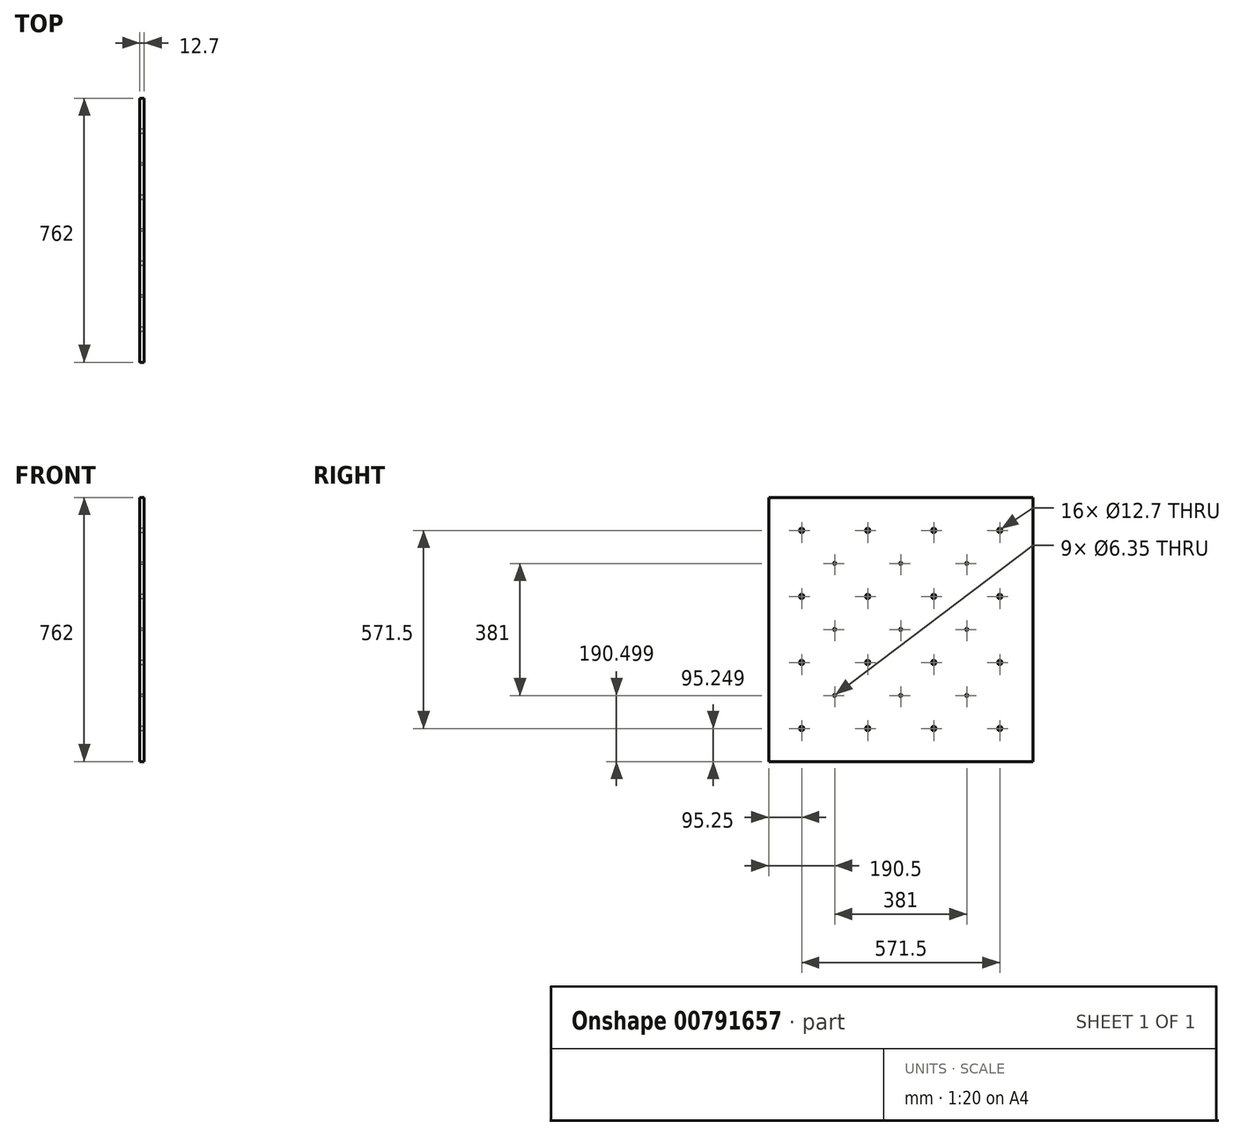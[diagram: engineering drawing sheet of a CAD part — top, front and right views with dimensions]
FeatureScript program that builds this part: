
annotation { "Feature Type Name" : "Feature", "Feature Type Description" : "" }
export const myFeature = defineFeature(function(context is Context, id is Id, definition is map)
    precondition{}
    {
        {
            var Q0;
            Q0=qCreatedBy(makeId("Right.planeOp"),FACE);
            var sketch = newSketch(context, id + "F0", { "sketchPlane" : qUnion([Q0])});
            skLineSegment(sketch, "E0", {"start": v(-381, 347.7) * mm, "end": v(381, 347.7) * mm});
            skLineSegment(sketch, "E1", {"start": v(381, 347.7) * mm, "end": v(381, -414.3) * mm});
            skLineSegment(sketch, "E2", {"start": v(381, -414.3) * mm, "end": v(-381, -414.3) * mm});
            skLineSegment(sketch, "E3", {"start": v(-381, 347.7) * mm, "end": v(-381, -414.3) * mm});
            skPoint(sketch, "E4", {"position": v(-285.75, 252.46) * mm});
            skPoint(sketch, "E5", {"position": v(285.75, 252.46) * mm});
            skPoint(sketch, "E6", {"position": v(-95.25, 252.46) * mm});
            skPoint(sketch, "E7", {"position": v(95.25, 252.46) * mm});
            skPoint(sketch, "E8", {"position": v(-285.75, 61.96) * mm});
            skPoint(sketch, "E9", {"position": v(-285.75, -128.54) * mm});
            skPoint(sketch, "E10", {"position": v(-285.75, -319.04) * mm});
            skPoint(sketch, "E11", {"position": v(-95.25, 61.96) * mm});
            skPoint(sketch, "E12", {"position": v(-95.25, -128.54) * mm});
            skPoint(sketch, "E13", {"position": v(-95.25, -319.04) * mm});
            skPoint(sketch, "E14", {"position": v(95.25, 61.96) * mm});
            skPoint(sketch, "E15", {"position": v(95.25, -128.54) * mm});
            skPoint(sketch, "E16", {"position": v(95.25, -319.04) * mm});
            skPoint(sketch, "E17", {"position": v(285.75, 61.96) * mm});
            skPoint(sketch, "E18", {"position": v(285.75, -128.54) * mm});
            skPoint(sketch, "E19", {"position": v(285.75, -319.04) * mm});
            skCircle(sketch, "E20", {"center": v(-285.75, 252.46) * mm, "radius": 6.35 * mm});
            skCircle(sketch, "E21", {"center": v(-95.25, 252.46) * mm, "radius": 6.35 * mm});
            skCircle(sketch, "E22", {"center": v(95.25, 252.46) * mm, "radius": 6.35 * mm});
            skCircle(sketch, "E23", {"center": v(285.75, 252.46) * mm, "radius": 6.35 * mm});
            skCircle(sketch, "E24", {"center": v(-285.75, 61.96) * mm, "radius": 6.35 * mm});
            skCircle(sketch, "E25", {"center": v(-95.25, 61.96) * mm, "radius": 6.35 * mm});
            skCircle(sketch, "E26", {"center": v(95.25, 61.96) * mm, "radius": 6.35 * mm});
            skCircle(sketch, "E27", {"center": v(285.75, 61.96) * mm, "radius": 6.35 * mm});
            skCircle(sketch, "E28", {"center": v(-285.75, -128.54) * mm, "radius": 6.35 * mm});
            skCircle(sketch, "E29", {"center": v(-95.25, -128.54) * mm, "radius": 6.35 * mm});
            skCircle(sketch, "E30", {"center": v(95.25, -128.54) * mm, "radius": 6.35 * mm});
            skCircle(sketch, "E31", {"center": v(285.75, -128.54) * mm, "radius": 6.35 * mm});
            skCircle(sketch, "E32", {"center": v(285.75, -319.04) * mm, "radius": 6.35 * mm});
            skCircle(sketch, "E33", {"center": v(95.25, -319.04) * mm, "radius": 6.35 * mm});
            skCircle(sketch, "E34", {"center": v(-95.25, -319.04) * mm, "radius": 6.35 * mm});
            skCircle(sketch, "E35", {"center": v(-285.75, -319.04) * mm, "radius": 6.35 * mm});
            skCircle(sketch, "E36", {"center": v(-190.5, 157.2) * mm, "radius": 3.18 * mm});
            skCircle(sketch, "E37", {"center": v(0, 157.2) * mm, "radius": 3.18 * mm});
            skCircle(sketch, "E38", {"center": v(190.5, 157.2) * mm, "radius": 3.18 * mm});
            skCircle(sketch, "E39", {"center": v(190.5, -33.3) * mm, "radius": 3.18 * mm});
            skCircle(sketch, "E40", {"center": v(190.5, -223.8) * mm, "radius": 3.18 * mm});
            skCircle(sketch, "E41", {"center": v(0, -223.8) * mm, "radius": 3.18 * mm});
            skCircle(sketch, "E42", {"center": v(-190.5, -223.8) * mm, "radius": 3.18 * mm});
            skCircle(sketch, "E43", {"center": v(-190.5, -33.3) * mm, "radius": 3.18 * mm});
            skCircle(sketch, "E44", {"center": v(0, -33.3) * mm, "radius": 3.18 * mm});
            skSolve(sketch);
        }
        {
            var Q0;
            Q0=makeQuery(id+"F0.imprint","IMPRINT",FACE,{"disambiguationData":[TD([[makeQuery(id+"F0.imprint","IMPRINT",EDGE,{"derivedFrom":sQuery(id+"F0.wireOp",EDGE,"E0")}),-1.0]])]});
            extrude(context, id + "F1", {"entities" : qUnion([Q0]), "depth" : 12.7 * mm, "offsetDistance" : 25.4 * mm});
        }
        {
            var Q0;
            Q0=sQuery(id+"F0.wireOp",EDGE,"E20");
            extrude(context, id + "F2", {"bodyType" : ToolBodyType.SURFACE, "surfaceEntities" : qUnion([Q0]), "depth" : 368.3 * mm, "offsetDistance" : 25.4 * mm});
        }
        {
            var Q0;
            Q0=sQuery(id+"F0.wireOp",EDGE,"E21");
            extrude(context, id + "F3", {"bodyType" : ToolBodyType.SURFACE, "surfaceEntities" : qUnion([Q0]), "depth" : 368.3 * mm, "offsetDistance" : 25.4 * mm});
        }
        {
            var Q0;
            Q0=sQuery(id+"F0.wireOp",EDGE,"E22");
            var Q1;
            Q1=sQuery(id+"F0.wireOp",EDGE,"E23");
            var Q2;
            Q2=sQuery(id+"F0.wireOp",EDGE,"E24");
            var Q3;
            Q3=sQuery(id+"F0.wireOp",EDGE,"E25");
            var Q4;
            Q4=sQuery(id+"F0.wireOp",EDGE,"E26");
            var Q5;
            Q5=sQuery(id+"F0.wireOp",EDGE,"E27");
            var Q6;
            Q6=sQuery(id+"F0.wireOp",EDGE,"E28");
            var Q7;
            Q7=sQuery(id+"F0.wireOp",EDGE,"E29");
            var Q8;
            Q8=sQuery(id+"F0.wireOp",EDGE,"E30");
            var Q9;
            Q9=sQuery(id+"F0.wireOp",EDGE,"E31");
            var Q10;
            Q10=sQuery(id+"F0.wireOp",EDGE,"E32");
            var Q11;
            Q11=sQuery(id+"F0.wireOp",EDGE,"E33");
            var Q12;
            Q12=sQuery(id+"F0.wireOp",EDGE,"E34");
            var Q13;
            Q13=sQuery(id+"F0.wireOp",EDGE,"E35");
            extrude(context, id + "F4", {"bodyType" : ToolBodyType.SURFACE, "surfaceEntities" : qUnion([Q0, Q1, Q2, Q3, Q4, Q5, Q6, Q7, Q8, Q9, Q10, Q11, Q12, Q13]), "depth" : 368.3 * mm, "offsetDistance" : 25.4 * mm});
        }
        {
            var Q0;
            Q0=sQuery(id+"F0.wireOp",EDGE,"E36");
            var Q1;
            Q1=sQuery(id+"F0.wireOp",EDGE,"E37");
            var Q2;
            Q2=sQuery(id+"F0.wireOp",EDGE,"E38");
            var Q3;
            Q3=sQuery(id+"F0.wireOp",EDGE,"E43");
            var Q4;
            Q4=sQuery(id+"F0.wireOp",EDGE,"E44");
            var Q5;
            Q5=sQuery(id+"F0.wireOp",EDGE,"E39");
            var Q6;
            Q6=sQuery(id+"F0.wireOp",EDGE,"E40");
            var Q7;
            Q7=sQuery(id+"F0.wireOp",EDGE,"E41");
            var Q8;
            Q8=sQuery(id+"F0.wireOp",EDGE,"E42");
            extrude(context, id + "F5", {"bodyType" : ToolBodyType.SURFACE, "surfaceEntities" : qUnion([Q0, Q1, Q2, Q3, Q4, Q5, Q6, Q7, Q8]), "depth" : 139.7 * mm, "offsetDistance" : 25.4 * mm});
        }
    });
